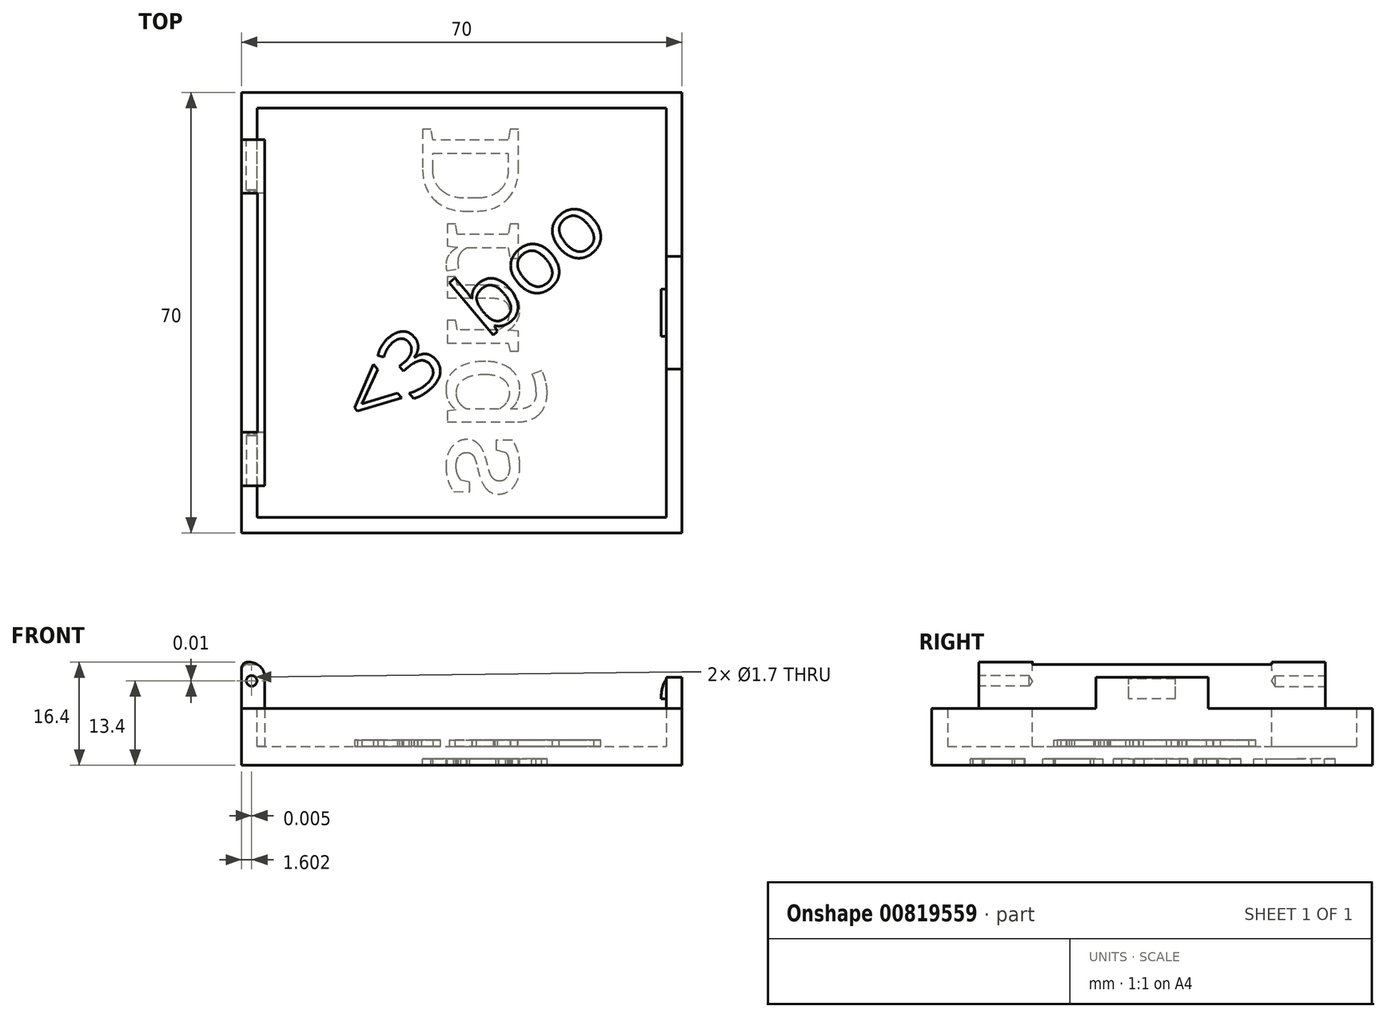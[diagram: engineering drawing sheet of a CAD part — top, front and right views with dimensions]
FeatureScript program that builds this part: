
annotation { "Feature Type Name" : "Feature", "Feature Type Description" : "" }
export const myFeature = defineFeature(function(context is Context, id is Id, definition is map)
    precondition{}
    {
        {
            var Q0;
            Q0=qCreatedBy(makeId("Top.planeOp"),FACE);
            var sketch = newSketch(context, id + "F0", { "sketchPlane" : qUnion([Q0])});
            skLineSegment(sketch, "E0.bottom", {"start": v(-37.36, -39.62) * mm, "end": v(27.64, -39.62) * mm});
            skLineSegment(sketch, "E0.top", {"start": v(-37.36, 25.38) * mm, "end": v(27.64, 25.38) * mm});
            skLineSegment(sketch, "E0.left", {"start": v(-37.36, -39.62) * mm, "end": v(-37.36, 25.38) * mm});
            skLineSegment(sketch, "E0.right", {"start": v(27.64, -39.62) * mm, "end": v(27.64, 25.38) * mm});
            skLineSegment(sketch, "E1.bottom", {"start": v(-39.86, 27.88) * mm, "end": v(30.14, 27.88) * mm});
            skLineSegment(sketch, "E1.top", {"start": v(-39.86, -42.12) * mm, "end": v(30.14, -42.12) * mm});
            skLineSegment(sketch, "E1.left", {"start": v(-39.86, 27.88) * mm, "end": v(-39.86, -42.12) * mm});
            skLineSegment(sketch, "E1.right", {"start": v(30.14, 27.88) * mm, "end": v(30.14, -42.12) * mm});
            skSolve(sketch);
        }
        {
            var Q0;
            Q0=makeQuery(id+"F0.imprint","IMPRINT",FACE,{"disambiguationData":[TD([[makeQuery(id+"F0.imprint","IMPRINT",EDGE,{"derivedFrom":sQuery(id+"F0.wireOp",EDGE,"E0.bottom")}),-1.0]])]});
            extrude(context, id + "F1", {"entities" : qUnion([Q0]), "depth" : 8 * mm, "offsetDistance" : 25 * mm});
        }
        {
            var Q0;
            Q0=makeQuery(id+"F0.imprint","IMPRINT",FACE,{"disambiguationData":[TD([[makeQuery(id+"F0.imprint","IMPRINT",EDGE,{"derivedFrom":sQuery(id+"F0.wireOp",EDGE,"E0.bottom")}),1.0]])]});
            extrude(context, id + "F2", {"entities" : qUnion([Q0]), "operationType" : NewBodyOperationType.ADD, "depth" : 2 * mm, "offsetDistance" : 25 * mm});
        }
        {
            var Q0;
            Q0=makeQuery(id+"F1.opExtrude","CAP_FACE",FACE,{"disambiguationData":[OSD([sQuery(id+"F0.wireOp",EDGE,"E0.bottom"),sQuery(id+"F0.wireOp",EDGE,"E0.top"),sQuery(id+"F0.wireOp",EDGE,"E0.left"),sQuery(id+"F0.wireOp",EDGE,"E0.right"),sQuery(id+"F0.wireOp",EDGE,"E1.bottom"),sQuery(id+"F0.wireOp",EDGE,"E1.top"),sQuery(id+"F0.wireOp",EDGE,"E1.left"),sQuery(id+"F0.wireOp",EDGE,"E1.right")])],"isStart":false});
            var sketch = newSketch(context, id + "F3", { "sketchPlane" : qUnion([Q0])});
            skLineSegment(sketch, "E2.bottom", {"start": v(30.14, -16.06) * mm, "end": v(27.64, -16.06) * mm});
            skLineSegment(sketch, "E2.top", {"start": v(30.14, 1.82) * mm, "end": v(27.64, 1.82) * mm});
            skLineSegment(sketch, "E2.left", {"start": v(30.14, -16.06) * mm, "end": v(30.14, 1.82) * mm});
            skLineSegment(sketch, "E2.right", {"start": v(27.64, -16.06) * mm, "end": v(27.64, 1.82) * mm});
            skPoint(sketch, "E3", {"position": v(30.14, -7.12) * mm});
            skSolve(sketch);
        }
        {
            var Q0;
            Q0=makeQuery(id+"F3.imprint","IMPRINT",FACE,{"disambiguationData":[TD([[makeQuery(id+"F3.imprint","IMPRINT",EDGE,{"derivedFrom":sQuery(id+"F3.wireOp",EDGE,"E2.bottom")}),-1.0]])]});
            extrude(context, id + "F4", {"entities" : qUnion([Q0]), "operationType" : NewBodyOperationType.ADD, "depth" : 5 * mm, "offsetDistance" : 25 * mm});
        }
        {
            var Q0;
            Q0=makeQuery(id+"F4.boolean.opBoolean","MERGE",FACE,{"derivedFrom":[makeQuery(id+"F1.opExtrude","SWEPT_FACE",FACE,{"disambiguationData":[OSD([sQuery(id+"F0.wireOp",EDGE,"E0.right")])]}),makeQuery(id+"F4.opExtrude","SWEPT_FACE",FACE,{"disambiguationData":[OSD([sQuery(id+"F3.wireOp",EDGE,"E2.right")])]})]});
            var sketch = newSketch(context, id + "F5", { "sketchPlane" : qUnion([Q0])});
            skLineSegment(sketch, "E4.bottom", {"start": v(3.38, 9.55) * mm, "end": v(10.86, 9.55) * mm});
            skLineSegment(sketch, "E4.top", {"start": v(3.38, 12.75) * mm, "end": v(10.86, 12.75) * mm});
            skLineSegment(sketch, "E4.left", {"start": v(3.38, 9.55) * mm, "end": v(3.38, 12.75) * mm});
            skLineSegment(sketch, "E4.right", {"start": v(10.86, 9.55) * mm, "end": v(10.86, 12.75) * mm});
            skSolve(sketch);
        }
        {
            var Q0;
            Q0=makeQuery(id+"F5.imprint","IMPRINT",FACE,{"disambiguationData":[TD([[makeQuery(id+"F5.imprint","IMPRINT",EDGE,{"derivedFrom":sQuery(id+"F5.wireOp",EDGE,"E4.bottom")}),1.0]])]});
            extrude(context, id + "F6", {"entities" : qUnion([Q0]), "operationType" : NewBodyOperationType.ADD, "depth" : .8 * mm, "offsetDistance" : 25 * mm});
        }
        {
            var Q0;
            Q0=makeQuery(id+"F6.opExtrude","CAP_EDGE",EDGE,{"disambiguationData":[OSD([sQuery(id+"F5.wireOp",EDGE,"E4.top")])],"isStart":false});
            fillet(context, id + "F7", {"entities" : qUnion([Q0]), "radius" : 5 * mm, "tangentPropagation" : true, "allowEdgeOverflow" : false});
        }
        {
            var Q0;
            Q0=makeQuery(id+"F1.opExtrude","CAP_FACE",FACE,{"disambiguationData":[OSD([sQuery(id+"F0.wireOp",EDGE,"E0.bottom"),sQuery(id+"F0.wireOp",EDGE,"E0.top"),sQuery(id+"F0.wireOp",EDGE,"E0.left"),sQuery(id+"F0.wireOp",EDGE,"E0.right"),sQuery(id+"F0.wireOp",EDGE,"E1.bottom"),sQuery(id+"F0.wireOp",EDGE,"E1.top"),sQuery(id+"F0.wireOp",EDGE,"E1.left"),sQuery(id+"F0.wireOp",EDGE,"E1.right")])],"isStart":false});
            var sketch = newSketch(context, id + "F8", { "sketchPlane" : qUnion([Q0])});
            skLineSegment(sketch, "E5.bottom", {"start": v(-39.86, 11.88) * mm, "end": v(-36.16, 11.88) * mm});
            skLineSegment(sketch, "E5.top", {"start": v(-39.86, -26.12) * mm, "end": v(-36.16, -26.12) * mm});
            skLineSegment(sketch, "E5.left", {"start": v(-39.86, 11.88) * mm, "end": v(-39.86, -26.12) * mm});
            skLineSegment(sketch, "E5.right", {"start": v(-36.16, 11.88) * mm, "end": v(-36.16, -26.12) * mm});
            skSolve(sketch);
        }
        {
            var Q0;
            {var subQ0=sQuery(id+"F8.wireOp",EDGE,"E5.right");Q0=makeQuery(id+"F8.imprint","IMPRINT",FACE,{"disambiguationData":[TD([[makeQuery(id+"F8.imprint","IMPRINT",EDGE,{"derivedFrom":subQ0}),-1.0]])]});}
            var Q1;
            {var subQ0=sQuery(id+"F8.wireOp",EDGE,"E5.left");Q1=makeQuery(id+"F8.imprint","IMPRINT",FACE,{"disambiguationData":[TD([[makeQuery(id+"F8.imprint","IMPRINT",EDGE,{"derivedFrom":subQ0}),1.0]])]});}
            extrude(context, id + "F9", {"entities" : qUnion([Q0, Q1]), "operationType" : NewBodyOperationType.ADD, "depth" : 7 * mm, "offsetDistance" : 25 * mm});
        }
        {
            var Q0;
            {var subQ0=sQuery(id+"F8.wireOp",EDGE,"E5.right");Q0=makeQuery(id+"F8.imprint","IMPRINT",FACE,{"disambiguationData":[TD([[makeQuery(id+"F8.imprint","IMPRINT",EDGE,{"derivedFrom":subQ0}),-1.0]])]});}
            extrude(context, id + "F10", {"entities" : qUnion([Q0]), "operationType" : NewBodyOperationType.ADD, "endBound" : BoundingType.UP_TO_NEXT, "oppositeDirection" : true, "depth" : 5 * mm, "offsetDistance" : 25 * mm});
        }
        {
            var Q0;
            {var subQ0=sQuery(id+"F0.wireOp",EDGE,"E0.top");var subQ1=sQuery(id+"F0.wireOp",EDGE,"E1.right");var subQ2=sQuery(id+"F0.wireOp",EDGE,"E1.left");var subQ3=sQuery(id+"F0.wireOp",EDGE,"E0.left");var subQ5=sQuery(id+"F0.wireOp",EDGE,"E0.right");var subQ6=sQuery(id+"F0.wireOp",EDGE,"E1.bottom");Q0=makeQuery(id+"F9.boolean.opBoolean","SPLIT",FACE,{"disambiguationData":[TD([makeQuery(id+"F1.opExtrude","SWEPT_FACE",FACE,{"disambiguationData":[OSD([subQ0])]})])],"derivedFrom":makeQuery(id+"F1.opExtrude","CAP_FACE",FACE,{"disambiguationData":[OSD([sQuery(id+"F0.wireOp",EDGE,"E0.bottom"),subQ0,subQ3,subQ5,subQ6,sQuery(id+"F0.wireOp",EDGE,"E1.top"),subQ2,subQ1])],"isStart":false})});}
            var sketch = newSketch(context, id + "F11", { "sketchPlane" : qUnion([Q0])});
            skLineSegment(sketch, "E6.bottom", {"start": v(-39.86, 20.38) * mm, "end": v(-36.16, 20.38) * mm});
            skLineSegment(sketch, "E6.top", {"start": v(-39.86, 11.88) * mm, "end": v(-36.16, 11.88) * mm});
            skLineSegment(sketch, "E6.left", {"start": v(-39.86, 20.38) * mm, "end": v(-39.86, 11.88) * mm});
            skLineSegment(sketch, "E6.right", {"start": v(-36.16, 20.38) * mm, "end": v(-36.16, 11.88) * mm});
            skLineSegment(sketch, "E7.bottom", {"start": v(-39.85, -26.11) * mm, "end": v(-36.15, -26.11) * mm});
            skLineSegment(sketch, "E7.top", {"start": v(-39.85, -34.61) * mm, "end": v(-36.15, -34.61) * mm});
            skLineSegment(sketch, "E7.left", {"start": v(-39.85, -26.11) * mm, "end": v(-39.85, -34.61) * mm});
            skLineSegment(sketch, "E7.right", {"start": v(-36.15, -26.11) * mm, "end": v(-36.15, -34.61) * mm});
            skSolve(sketch);
        }
        {
            var Q0;
            Q0 = qSketchRegion(id + "F11", true);
            extrude(context, id + "F12", {"entities" : qUnion([Q0]), "operationType" : NewBodyOperationType.ADD, "depth" : 7.4 * mm, "offsetDistance" : 25 * mm});
        }
        {
            var Q0;
            Q0=makeQuery(id+"F12.opExtrude","SWEPT_FACE",FACE,{"disambiguationData":[OSD([sQuery(id+"F11.wireOp",EDGE,"E6.bottom")])]});
            var sketch = newSketch(context, id + "F13", { "sketchPlane" : qUnion([Q0])});
            skPoint(sketch, "E8", {"position": v(38.26, 12.4) * mm});
            skPoint(sketch, "E9", {"position": v(14.71, -29.21) * mm});
            skPoint(sketch, "E10", {"position": v(38, 15.4) * mm});
            skSolve(sketch);
        }
        {
            var Q0;
            Q0=sQuery(id+"F13.wireOp",VERTEX,"E8");
            var Q1;
            Q1=makeQuery(id+"F1.opExtrude","SWEPT_BODY",BODY,{"disambiguationData":[OSD([sQuery(id+"F0.wireOp",EDGE,"E0.bottom"),sQuery(id+"F0.wireOp",EDGE,"E0.top"),sQuery(id+"F0.wireOp",EDGE,"E0.left"),sQuery(id+"F0.wireOp",EDGE,"E0.right"),sQuery(id+"F0.wireOp",EDGE,"E1.bottom"),sQuery(id+"F0.wireOp",EDGE,"E1.top"),sQuery(id+"F0.wireOp",EDGE,"E1.left"),sQuery(id+"F0.wireOp",EDGE,"E1.right")])]});
            hole(context, id + "F14", {"style" : HoleStyle.SIMPLE, "endStyle" : HoleEndStyle.BLIND, "holeDiameter" : 1.7 * mm, "majorDiameter" : 5 * mm, "holeDepth" : 8 * mm, "isTappedThrough" : true, "tappedDepth" : 12 * mm, "tapClearance" : 3, "locations" : qUnion([Q0]), "scope" : qUnion([Q1])});
        }
        {
            var Q0;
            Q0=makeQuery(id+"F12.opExtrude","SWEPT_FACE",FACE,{"disambiguationData":[OSD([sQuery(id+"F11.wireOp",EDGE,"E7.top")])]});
            var sketch = newSketch(context, id + "F15", { "sketchPlane" : qUnion([Q0])});
            skPoint(sketch, "E11", {"position": v(-38.25, 12.41) * mm});
            skPoint(sketch, "E12", {"position": v(-38, 15.4) * mm});
            skSolve(sketch);
        }
        {
            var Q0;
            Q0=sQuery(id+"F15.wireOp",VERTEX,"E11");
            var Q1;
            Q1=makeQuery(id+"F1.opExtrude","SWEPT_BODY",BODY,{"disambiguationData":[OSD([sQuery(id+"F0.wireOp",EDGE,"E0.bottom"),sQuery(id+"F0.wireOp",EDGE,"E0.top"),sQuery(id+"F0.wireOp",EDGE,"E0.left"),sQuery(id+"F0.wireOp",EDGE,"E0.right"),sQuery(id+"F0.wireOp",EDGE,"E1.bottom"),sQuery(id+"F0.wireOp",EDGE,"E1.top"),sQuery(id+"F0.wireOp",EDGE,"E1.left"),sQuery(id+"F0.wireOp",EDGE,"E1.right")])]});
            hole(context, id + "F16", {"style" : HoleStyle.SIMPLE, "endStyle" : HoleEndStyle.BLIND, "holeDiameter" : 1.7 * mm, "majorDiameter" : 5 * mm, "holeDepth" : 8 * mm, "isTappedThrough" : true, "tappedDepth" : 12 * mm, "tapClearance" : 3, "locations" : qUnion([Q0]), "scope" : qUnion([Q1])});
        }
        {
            var Q0;
            {var subQ0=sQuery(id+"F0.wireOp",EDGE,"E0.right");var subQ1=sQuery(id+"F0.wireOp",EDGE,"E0.left");var subQ2=sQuery(id+"F0.wireOp",EDGE,"E0.top");var subQ3=sQuery(id+"F0.wireOp",EDGE,"E0.bottom");Q0=makeQuery(id+"F2.boolean.opBoolean","MERGE",FACE,{"derivedFrom":[makeQuery(id+"F1.opExtrude","CAP_FACE",FACE,{"disambiguationData":[OSD([subQ3,subQ2,subQ1,subQ0,sQuery(id+"F0.wireOp",EDGE,"E1.bottom"),sQuery(id+"F0.wireOp",EDGE,"E1.top"),sQuery(id+"F0.wireOp",EDGE,"E1.left"),sQuery(id+"F0.wireOp",EDGE,"E1.right")])],"isStart":true}),makeQuery(id+"F2.opExtrude","CAP_FACE",FACE,{"disambiguationData":[OSD([subQ3,subQ2,subQ1,subQ0])],"isStart":true})]});}
            var sketch = newSketch(context, id + "F17", { "sketchPlane" : qUnion([Q0])});
            skText(sketch, "E13", { "text": "Drugs", "fontName": "RobotoSlab-Regular.ttf"});
            const initialGuessF17  = {"E13": [0.00413, -0.02273, 0, 1, 0.0154]};
            skSetInitialGuess(sketch, initialGuessF17);
            skSolve(sketch);
        }
        {
            var Q0;
            Q0=makeQuery(id+"F17.imprint","IMPRINT",FACE,{"disambiguationData":[TD([[makeQuery(id+"F17.imprint","IMPRINT",EDGE,{"derivedFrom":sQuery(id+"F17.wireOp",EDGE,"E13.sketch_text.stroke-0")}),1.0]])]});
            var Q1;
            Q1=makeQuery(id+"F17.imprint","IMPRINT",FACE,{"disambiguationData":[TD([[makeQuery(id+"F17.imprint","IMPRINT",EDGE,{"derivedFrom":sQuery(id+"F17.wireOp",EDGE,"E13.sketch_text.stroke-86")}),1.0]])]});
            var Q2;
            Q2=makeQuery(id+"F17.imprint","IMPRINT",FACE,{"disambiguationData":[TD([[makeQuery(id+"F17.imprint","IMPRINT",EDGE,{"derivedFrom":sQuery(id+"F17.wireOp",EDGE,"E13.sketch_text.stroke-13")}),1.0]])]});
            var Q3;
            {var subQ0=sQuery(id+"F0.wireOp",EDGE,"E0.top");var subQ1=sQuery(id+"F0.wireOp",EDGE,"E1.right");var subQ2=sQuery(id+"F0.wireOp",EDGE,"E1.left");var subQ3=sQuery(id+"F0.wireOp",EDGE,"E0.left");var subQ5=sQuery(id+"F0.wireOp",EDGE,"E0.right");var subQ6=sQuery(id+"F0.wireOp",EDGE,"E1.bottom");Q3=makeQuery(id+"F9.boolean.opBoolean","SPLIT",FACE,{"disambiguationData":[TD([makeQuery(id+"F1.opExtrude","SWEPT_FACE",FACE,{"disambiguationData":[OSD([subQ0])]})])],"derivedFrom":makeQuery(id+"F1.opExtrude","CAP_FACE",FACE,{"disambiguationData":[OSD([sQuery(id+"F0.wireOp",EDGE,"E0.bottom"),subQ0,subQ3,subQ5,subQ6,sQuery(id+"F0.wireOp",EDGE,"E1.top"),subQ2,subQ1])],"isStart":false})});}
            var Q4;
            Q4 = qConstructionFilter(qBodyType(qCreatedBy(id + "F17" ,EDGE), BodyType.WIRE), ConstructionObject.NO);
            extrude(context, id + "F18", {"entities" : qUnion([Q0, Q1, Q2, Q3]), "operationType" : NewBodyOperationType.ADD, "surfaceOperationType" : NewSurfaceOperationType.ADD, "surfaceEntities" : qUnion([Q4]), "depth" : 1 * mm, "offsetDistance" : 25 * mm});
        }
        {
            var Q0;
            Q0=makeQuery(id+"F2.opExtrude","CAP_FACE",FACE,{"disambiguationData":[OSD([sQuery(id+"F0.wireOp",EDGE,"E0.bottom"),sQuery(id+"F0.wireOp",EDGE,"E0.top"),sQuery(id+"F0.wireOp",EDGE,"E0.left"),sQuery(id+"F0.wireOp",EDGE,"E0.right")])],"isStart":false});
            var sketch = newSketch(context, id + "F19", { "sketchPlane" : qUnion([Q0])});
            skText(sketch, "E14", { "text": "<3  boo", "fontName": "OpenSans-Regular.ttf"});
            skLineSegment(sketch, "E15.0", {"start": v(-19.03, -26.77) * mm, "end": v(19.28, 5.37) * mm, "construction": true});
            skLineSegment(sketch, "E15.1", {"start": v(-19.03, -26.77) * mm, "end": v(-19.03, -26.77) * mm});
            const initialGuessF19  = {"E14": [-0.01903, -0.02677, 0.76604, 0.64279, 0.0103]};
            skSetInitialGuess(sketch, initialGuessF19);
            skSolve(sketch);
        }
        {
            var Q0;
            Q0 = qSketchRegion(id + "F19", true);
            extrude(context, id + "F20", {"entities" : qUnion([Q0]), "operationType" : NewBodyOperationType.ADD, "depth" : 1 * mm, "offsetDistance" : 25 * mm});
        }
        {
            var Q0;
            Q0=makeQuery(id+"F12.opExtrude","CAP_EDGE",EDGE,{"disambiguationData":[OSD([sQuery(id+"F11.wireOp",EDGE,"E7.right")])],"isStart":false});
            fillet(context, id + "F21", {"entities" : qUnion([Q0]), "radius" : 2.5 * mm, "tangentPropagation" : true, "allowEdgeOverflow" : false});
        }
        {
            var Q0;
            Q0=makeQuery(id+"F9.opExtrude","CAP_EDGE",EDGE,{"disambiguationData":[OSD([sQuery(id+"F8.wireOp",EDGE,"E5.left")])],"isStart":false});
            fillet(context, id + "F22", {"entities" : qUnion([Q0]), "radius" : 1 * mm, "tangentPropagation" : true, "allowEdgeOverflow" : false});
        }
        {
            var Q0;
            Q0=makeQuery(id+"F12.opExtrude","CAP_EDGE",EDGE,{"disambiguationData":[OSD([sQuery(id+"F11.wireOp",EDGE,"E7.left")])],"isStart":false});
            var Q1;
            Q1=makeQuery(id+"F12.opExtrude","CAP_EDGE",EDGE,{"disambiguationData":[OSD([sQuery(id+"F11.wireOp",EDGE,"E6.left")])],"isStart":false});
            fillet(context, id + "F23", {"entities" : qUnion([Q0, Q1]), "radius" : 1 * mm, "tangentPropagation" : true, "allowEdgeOverflow" : false});
        }
    });
